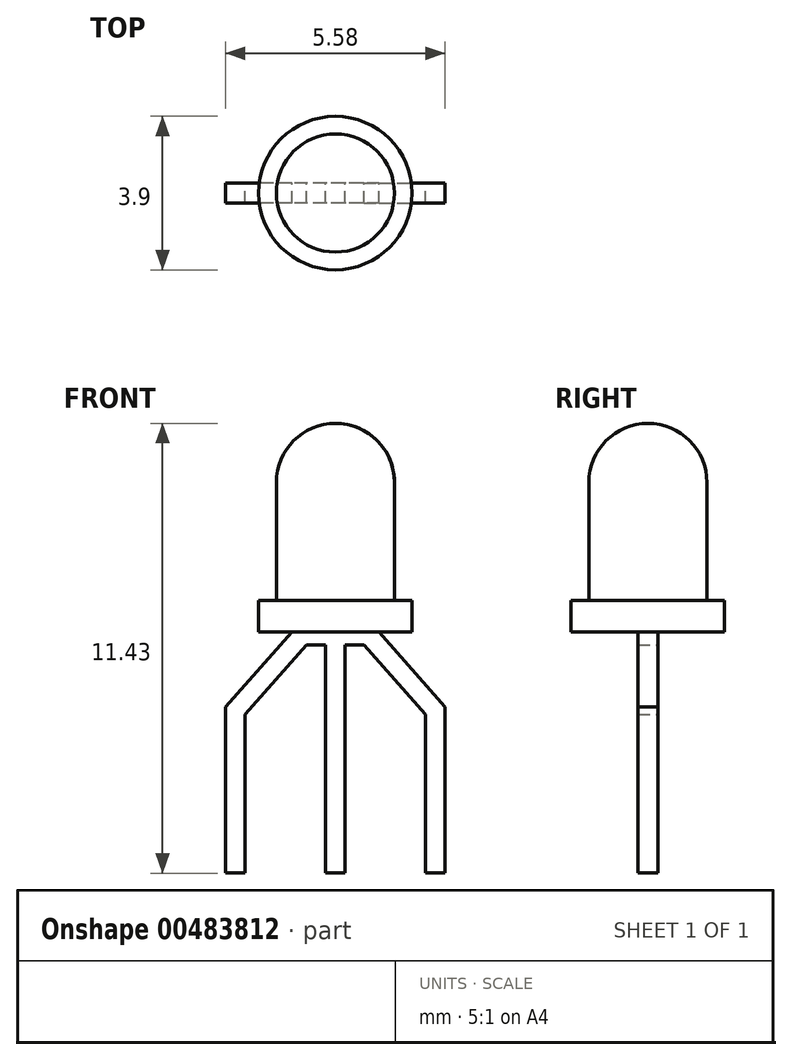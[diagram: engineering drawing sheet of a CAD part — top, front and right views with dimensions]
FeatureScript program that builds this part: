
annotation { "Feature Type Name" : "Feature", "Feature Type Description" : "" }
export const myFeature = defineFeature(function(context is Context, id is Id, definition is map)
    precondition{}
    {
        {
            var Q0;
            Q0=qCreatedBy(makeId("Top.planeOp"),FACE);
            var sketch = newSketch(context, id + "F0", { "sketchPlane" : qUnion([Q0])});
            skCircle(sketch, "E0", {"center": v(0, 0) * mm, "radius": 1.95 * mm});
            skSolve(sketch);
        }
        {
            var Q0;
            Q0=qSketchRegion(id+"F0",true);
            extrude(context, id + "F1", {"entities" : qUnion([Q0]), "depth" : .8 * mm});
        }
        {
            var Q0;
            Q0=makeQuery(id+"F1.opExtrude","CAP_FACE",FACE,{"disambiguationData":[OSD([sQuery(id+"F0.wireOp",EDGE,"E0")])],"isStart":false});
            var sketch = newSketch(context, id + "F2", { "sketchPlane" : qUnion([Q0])});
            skCircle(sketch, "E1", {"center": v(0, 0) * mm, "radius": 1.5 * mm});
            skSolve(sketch);
        }
        {
            var Q0;
            Q0=qSketchRegion(id+"F2",true);
            extrude(context, id + "F3", {"entities" : qUnion([Q0]), "operationType" : NewBodyOperationType.ADD, "depth" : 4.5 * mm});
        }
        {
            var Q0;
            Q0=makeQuery(id+"F3.opExtrude","CAP_EDGE",EDGE,{"disambiguationData":[OSD([sQuery(id+"F2.wireOp",EDGE,"E1")])],"isStart":false});
            fillet(context, id + "F4", {"entities" : qUnion([Q0]), "radius" : 1.5 * mm, "tangentPropagation" : true, "allowEdgeOverflow" : false});
        }
        {
            var Q0;
            Q0=qCreatedBy(makeId("Front.planeOp"),FACE);
            var sketch = newSketch(context, id + "F5", { "sketchPlane" : qUnion([Q0])});
            skLineSegment(sketch, "E2", {"start": v(0, -0.9) * mm, "end": v(0, -7.84) * mm});
            skLineSegment(sketch, "E3", {"start": v(-2.54, -0.9) * mm, "end": v(-2.54, -7.96) * mm});
            skLineSegment(sketch, "E4", {"start": v(2.54, -0.97) * mm, "end": v(2.54, -7.53) * mm});
            skLineSegment(sketch, "E5.0", {"start": v(2.29, -0.97) * mm, "end": v(2.3, -6.13) * mm});
            skLineSegment(sketch, "E6.0", {"start": v(2.8, -0.97) * mm, "end": v(2.8, -6.13) * mm});
            skLineSegment(sketch, "E7.0", {"start": v(-0.25, -0.33) * mm, "end": v(-0.25, -7.84) * mm});
            skLineSegment(sketch, "E8.0", {"start": v(0.25, -0.33) * mm, "end": v(0.25, -7.84) * mm});
            skLineSegment(sketch, "E9.0", {"start": v(-2.3, -0.9) * mm, "end": v(-2.3, -7.96) * mm});
            skLineSegment(sketch, "E10.0", {"start": v(-2.8, -0.9) * mm, "end": v(-2.79, -7.96) * mm});
            skLineSegment(sketch, "E11", {"start": v(1.1, 0) * mm, "end": v(2.8, -1.9) * mm});
            skLineSegment(sketch, "E12.MirrorCS", {"start": v(-1.1, 0) * mm, "end": v(-2.8, -1.9) * mm});
            skLineSegment(sketch, "E13.0", {"start": v(0.73, -0.33) * mm, "end": v(2.42, -2.24) * mm});
            skLineSegment(sketch, "E14.0", {"start": v(-0.73, -0.33) * mm, "end": v(-2.42, -2.24) * mm});
            skLineSegment(sketch, "E15", {"start": v(0.73, -0.33) * mm, "end": v(-0.73, -0.33) * mm});
            skLineSegment(sketch, "E16", {"start": v(1.1, 0) * mm, "end": v(-1.1, 0) * mm});
            skLineSegment(sketch, "E17", {"start": v(2.8, -6.13) * mm, "end": v(2.3, -6.13) * mm});
            skLineSegment(sketch, "E18.trimOffspring", {"start": v(-2.3, -6.13) * mm, "end": v(-2.8, -6.13) * mm});
            skLineSegment(sketch, "E19.trimOffspring", {"start": v(0.25, -6.13) * mm, "end": v(-0.25, -6.13) * mm});
            skSolve(sketch);
        }
        {
            var Q0;
            Q0=qSketchRegion(id+"F5",true);
            extrude(context, id + "F6", {"entities" : qUnion([Q0]), "depth" : .25 * mm, "hasSecondDirection" : true, "secondDirectionOppositeDirection" : true, "secondDirectionDepth" : .25 * mm});
        }
    });
